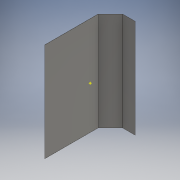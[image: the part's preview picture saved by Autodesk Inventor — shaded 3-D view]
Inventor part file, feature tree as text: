
AUTODESK INVENTOR PART (.ipt)
format: ipt  version: 2018 (Build 220112000, 112)  size: 121,856 bytes
history: native  units: mm
features: sheet_metal_op x3, other x2, sketch x1
ambient origin geometry x8: Origin, YZ Plane, XZ Plane, XY Plane, X Axis, Y Axis, Z Axis, Center Point
bodies: Solid1 (feature_tree)
feature tree (6):
  sheet_metal_op  "Contour Flange1"
  other  "Work Point1"
  sketch  "Sketch1"  dims[d2=135.0deg d3=154.0mm d4=1.6mm d5=1.6mm d6=0.8mm d7=3.2mm d8=1.6mm d9=1200.0mm d10=1.6mm d11=1.6mm d12=6.4mm d13=1.6mm d14=1.6mm d25=800.0mm d26=150.0mm d27=40.0mm]
  other  "Plate1"
  sheet_metal_op  "Bend1"
  sheet_metal_op  "Corner1"
